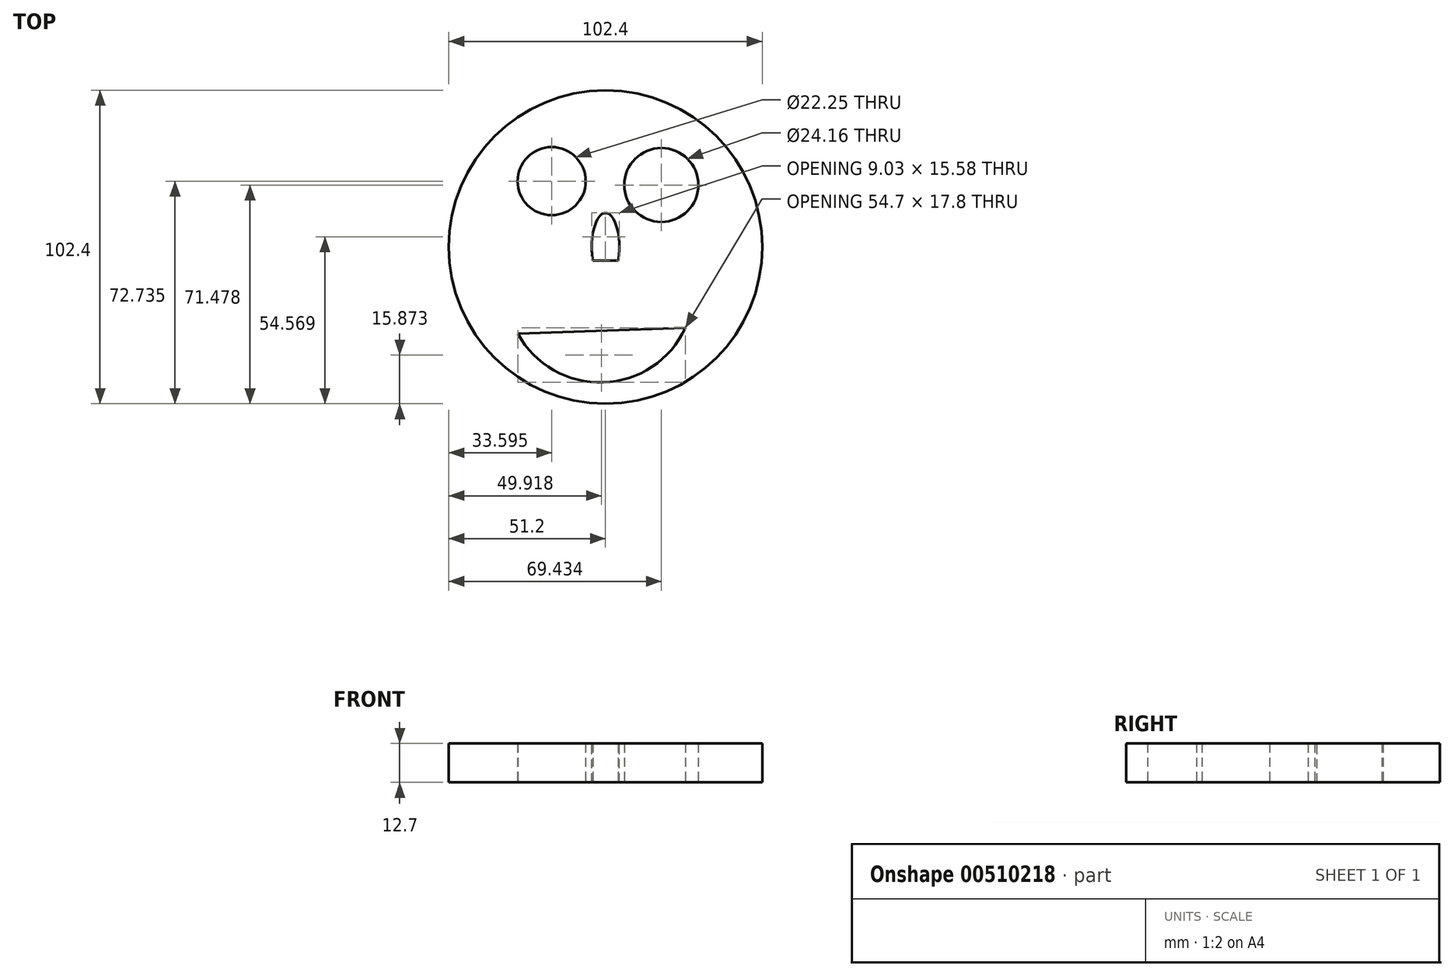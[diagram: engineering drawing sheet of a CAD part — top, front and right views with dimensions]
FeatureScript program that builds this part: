
annotation { "Feature Type Name" : "Feature", "Feature Type Description" : "" }
export const myFeature = defineFeature(function(context is Context, id is Id, definition is map)
    precondition{}
    {
        {
            var Q0;
            Q0=qCreatedBy(makeId("Top.planeOp"),FACE);
            var sketch = newSketch(context, id + "F0", { "sketchPlane" : qUnion([Q0])});
            skCircle(sketch, "E0", {"center": v(0, 0) * mm, "radius": 51.2 * mm});
            skCircle(sketch, "E1", {"center": v(-17.6, 21.54) * mm, "radius": 11.12 * mm});
            skCircle(sketch, "E2", {"center": v(18.23, 20.28) * mm, "radius": 12.08 * mm});
            skEllipticalArc(sketch, "E3", {});
            skLineSegment(sketch, "E4", {"start": v(-4.16, -4.42) * mm, "end": v(4.16, -4.42) * mm});
            skArc(sketch, "E5", {"start": v(-28.63, -28.31) * mm, "mid": v(-0.7, -44.23) * mm, "end": v(26.07, -26.43) * mm});
            skLineSegment(sketch, "E6", {"start": v(-28.63, -28.31) * mm, "end": v(26.07, -26.43) * mm});
            const initialGuessF0  = {"E3": [0, 0, 0, -1, 0.011160530149936676, 0.004533196673234628, 1.1634325355110915, 5.1197527716684945]};
            skSetInitialGuess(sketch, initialGuessF0);
            skSolve(sketch);
        }
        {
            var Q0;
            Q0=makeQuery(id+"F0.imprint","IMPRINT",FACE,{"disambiguationData":[TD([[makeQuery(id+"F0.imprint","IMPRINT",EDGE,{"derivedFrom":sQuery(id+"F0.wireOp",EDGE,"E0")}),1.0]])]});
            extrude(context, id + "F1", {"entities" : qUnion([Q0]), "depth" : 12.7 * mm});
        }
    });
